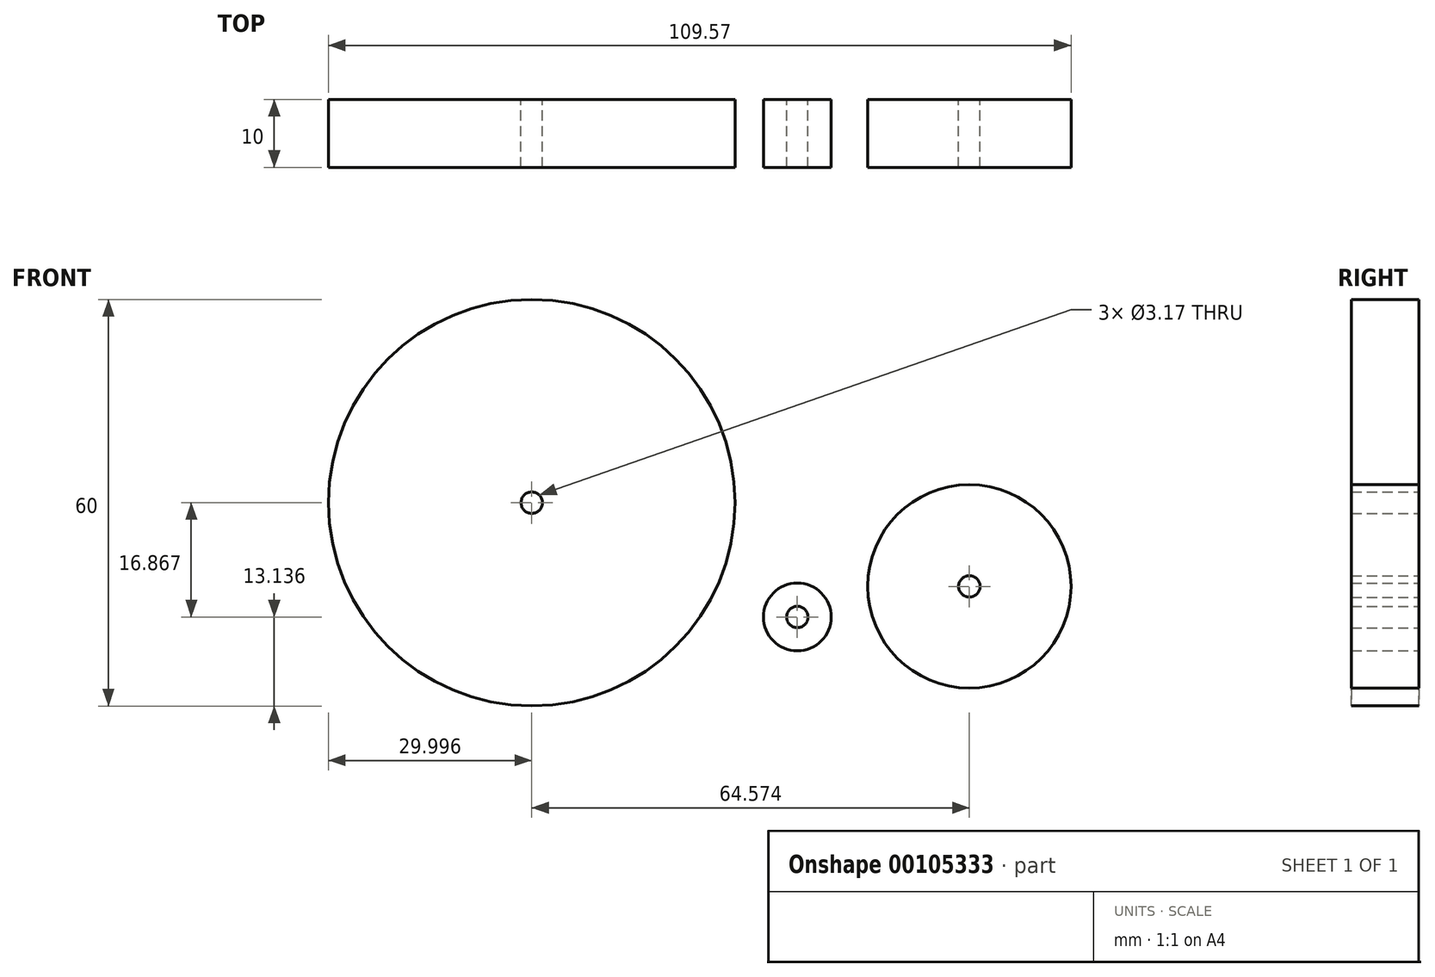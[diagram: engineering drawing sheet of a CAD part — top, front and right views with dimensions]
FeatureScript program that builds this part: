
annotation { "Feature Type Name" : "Feature", "Feature Type Description" : "" }
export const myFeature = defineFeature(function(context is Context, id is Id, definition is map)
    precondition{}
    {
        {
            var Q0;
            Q0=qCreatedBy(makeId("Front.planeOp"),FACE);
            var sketch = newSketch(context, id + "F0", { "sketchPlane" : qUnion([Q0])});
            skCircle(sketch, "E0", {"center": v(-47.6, 32.67) * mm, "radius": 30 * mm});
            skCircle(sketch, "E1", {"center": v(16.98, 20.32) * mm, "radius": 15 * mm});
            skCircle(sketch, "E2", {"center": v(-8.4, 15.8) * mm, "radius": 5 * mm});
            skCircle(sketch, "E3", {"center": v(-47.6, 32.67) * mm, "radius": 1.59 * mm});
            skCircle(sketch, "E4", {"center": v(-8.4, 15.8) * mm, "radius": 1.59 * mm});
            skCircle(sketch, "E5", {"center": v(16.98, 20.32) * mm, "radius": 0.88 * mm});
            skCircle(sketch, "E6", {"center": v(16.98, 20.32) * mm, "radius": 1.59 * mm});
            skSolve(sketch);
        }
        {
            var Q0;
            Q0 = qSketchRegion(id + "F0", true);
            extrude(context, id + "F1", {"entities" : qUnion([Q0]), "depth" : 10 * mm});
        }
    });
